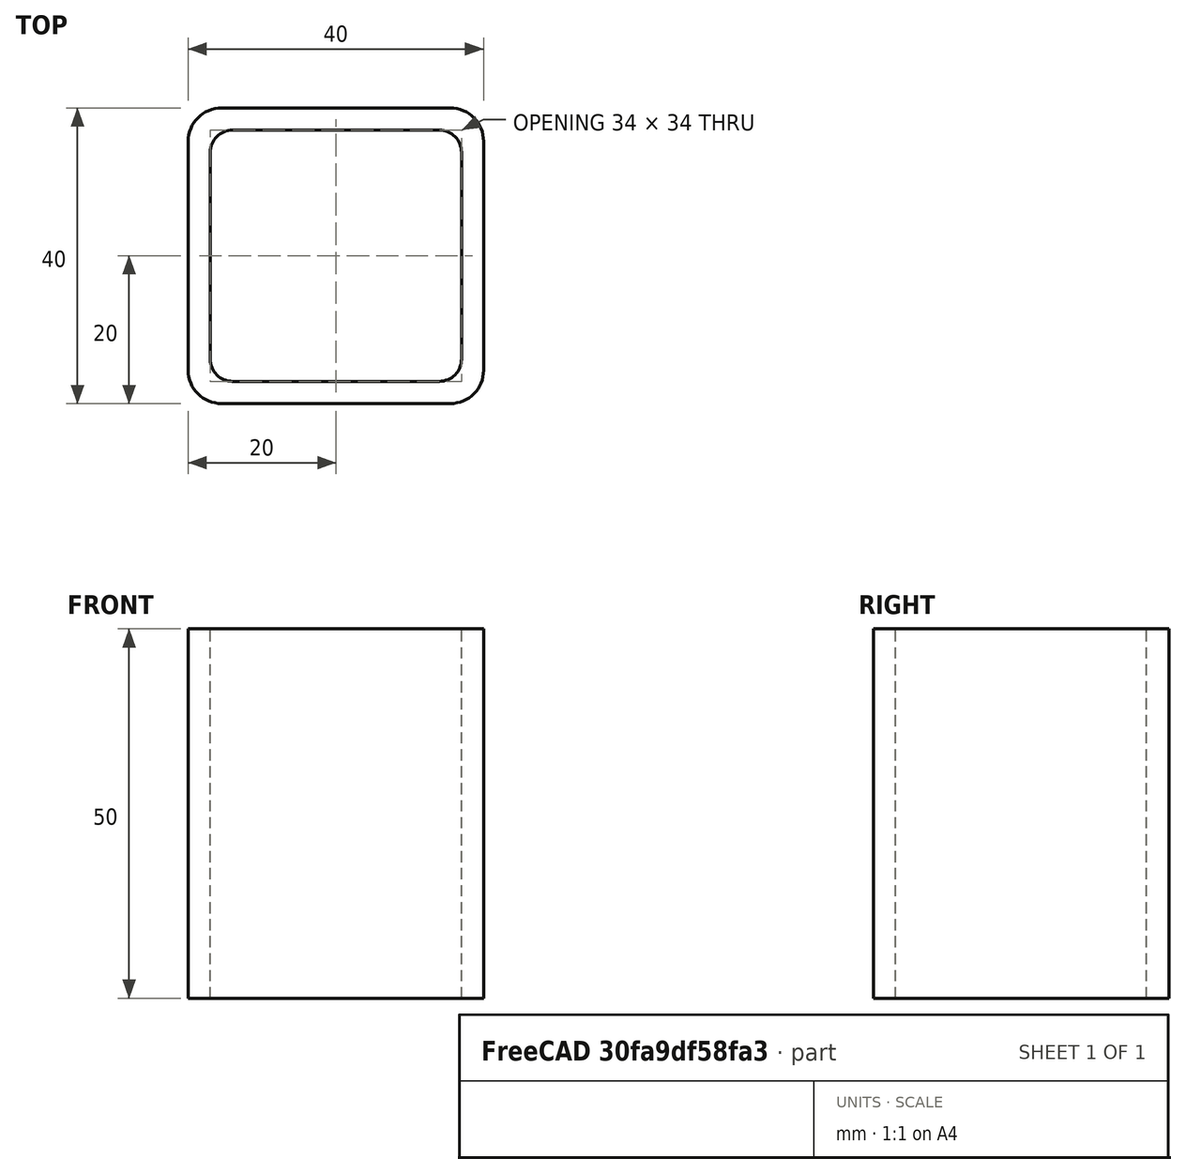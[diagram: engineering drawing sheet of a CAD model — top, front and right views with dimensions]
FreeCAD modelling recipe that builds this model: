
FCSTD DOCUMENT  (FreeCAD 0.15R4671 (Git))
Label: Square hollow section 40x40x3 EN10219 S235JRH
License: All rights reserved
LicenseURL: http://en.wikipedia.org/wiki/All_rights_reserved
objects: Sketcher::SketchObject×1, Part::Extrusion×1
note: 2 computed .brp shape members not serialized (recipe doc carries the construction recipe); baked Part::Feature solids carry a one-line shape summary decoded from their .brp

FEATURE [Sketcher::SketchObject] Sketch
  sketch-geometry (16):
    g0: LineSegment StartX=-14 StartY=17 StartZ=0 EndX=14 EndY=17 EndZ=0
    g1: LineSegment StartX=17 StartY=14 StartZ=0 EndX=17 EndY=-14 EndZ=0
    g2: LineSegment StartX=14 StartY=-17 StartZ=0 EndX=-14 EndY=-17 EndZ=0
    g3: LineSegment StartX=-17 StartY=-14 StartZ=0 EndX=-17 EndY=14 EndZ=0
    g4: LineSegment StartX=-15.5 StartY=20 StartZ=0 EndX=15.5 EndY=20 EndZ=0
    g5: LineSegment StartX=20 StartY=15.5 StartZ=0 EndX=20 EndY=-15.5 EndZ=0
    g6: LineSegment StartX=15.5 StartY=-20 StartZ=0 EndX=-15.5 EndY=-20 EndZ=0
    g7: LineSegment StartX=-20 StartY=-15.5 StartZ=0 EndX=-20 EndY=15.5 EndZ=0
    g8: ArcOfCircle CenterX=-14 CenterY=14 CenterZ=0 NormalX=0 NormalY=0 NormalZ=1 Radius=3 StartAngle=1.5708 EndAngle=3.14159
    g9: ArcOfCircle CenterX=14 CenterY=14 CenterZ=0 NormalX=0 NormalY=0 NormalZ=1 Radius=3 StartAngle=0 EndAngle=1.5708
    g10: ArcOfCircle CenterX=14 CenterY=-14 CenterZ=0 NormalX=0 NormalY=0 NormalZ=1 Radius=3 StartAngle=4.71239 EndAngle=6.28319
    g11: ArcOfCircle CenterX=-14 CenterY=-14 CenterZ=0 NormalX=0 NormalY=0 NormalZ=1 Radius=3 StartAngle=3.14159 EndAngle=4.71239
    g12: ArcOfCircle CenterX=15.5 CenterY=15.5 CenterZ=0 NormalX=0 NormalY=0 NormalZ=1 Radius=4.5 StartAngle=0 EndAngle=1.5708
    g13: ArcOfCircle CenterX=15.5 CenterY=-15.5 CenterZ=0 NormalX=0 NormalY=0 NormalZ=1 Radius=4.5 StartAngle=4.71239 EndAngle=6.28319
    g14: ArcOfCircle CenterX=-15.5 CenterY=-15.5 CenterZ=0 NormalX=0 NormalY=0 NormalZ=1 Radius=4.5 StartAngle=3.14159 EndAngle=4.71239
    g15: ArcOfCircle CenterX=-15.5 CenterY=15.5 CenterZ=0 NormalX=0 NormalY=0 NormalZ=1 Radius=4.5 StartAngle=1.5708 EndAngle=3.14159
  constraints (36):
    c: Horizontal(g2)
    c: Vertical(g3)
    c: Horizontal(g6)
    c: Vertical(g7)
    c: Tangent(g3,g8) = 1.5708
    c: Tangent(g0,g8) = 1.5708
    c: Tangent(g0,g9) = 1.5708
    c: Tangent(g1,g9) = 1.5708
    c: Tangent(g1,g10) = 1.5708
    c: Tangent(g2,g10) = 1.5708
    c: Tangent(g2,g11) = 1.5708
    c: Tangent(g3,g11) = 1.5708
    c: Tangent(g4,g12) = 1.5708
    c: Tangent(g5,g12) = 1.5708
    c: Tangent(g5,g13) = 1.5708
    c: Tangent(g6,g13) = 1.5708
    c: Tangent(g6,g14) = 1.5708
    c: Tangent(g7,g14) = 1.5708
    c: Tangent(g7,g15) = 1.5708
    c: Tangent(g4,g15) = 1.5708
    c: Equal(g9,g8)
    c: Equal(g9,g11)
    c: Equal(g9,g10)
    c: Equal(g12,g15)
    c: Equal(g12,g14)
    c: Equal(g12,g13)
    c: Symmetric(g4,g6,g-1)
    c: Symmetric(g7,g5,g-2)
    c: DistanceY(g4,g6) = -40
    c: DistanceX(g7,g5) = 40
    c: Symmetric(g3,g1,g-2)
    c: Symmetric(g0,g2,g-1)
    c: DistanceY(g0,g4) = 3
    c: DistanceX(g5,g1) = -3
    c: Radius(g9) = 3
    c: Radius(g12) = 4.5
FEATURE [Part::Extrusion] Extrude  label="Square hollow section 40x40x3 EN10219 S235JRH"
  Base = -> Sketch
  Dir = (0,0,50)
  Solid = true
